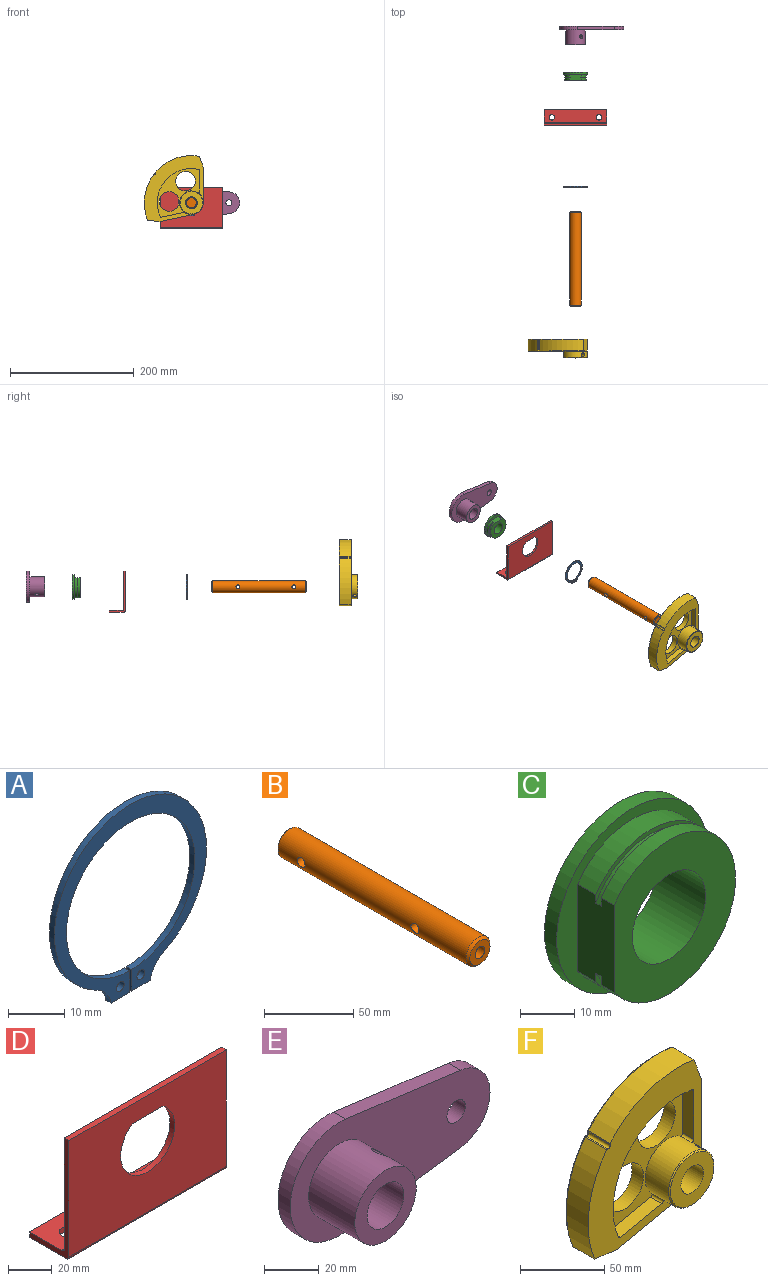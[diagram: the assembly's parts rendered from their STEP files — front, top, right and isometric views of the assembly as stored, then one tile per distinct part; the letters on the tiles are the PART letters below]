
ASSEMBLY  parts=6 mates=5
PART A: 12 faces, bbox 38.3x1.3x40.8 mm
  f0: cylinder r=19.13mm len=38.25mm, axis (0,1,0), area 131.2mm2, adj f1,f8,f10,f11
  f1: cylinder r=6.34mm len=4.3mm, axis (0,1,0), area 6.9mm2, adj f0,f2,f10,f11
  f2: plane 4.67x1.27mm, normal (0,0,-1), area 5.9mm2, adj f1,f3,f10,f11
  f3: plane 4.68x1.27mm, normal (1,0,0), area 5.9mm2, adj f2,f4,f10,f11
  f4: cylinder r=16.15mm len=32.31mm, axis (0,1,0), area 128.3mm2, adj f3,f5,f10,f11
  f5: plane 4.68x1.27mm, normal (-1,0,0), area 5.9mm2, adj f4,f6,f10,f11
  f6: plane 4.67x1.27mm, normal (0,0,-1), area 5.9mm2, adj f5,f8,f10,f11
  f7: cylinder r=0.99mm len=1.98mm, axis (0,1,0), area 7.9mm2, adj f10,f11
  f8: cylinder r=6.34mm len=4.54mm, axis (0,1,0), area 7.5mm2, adj f0,f6,f10,f11
  f9: cylinder r=0.99mm len=1.98mm, axis (0,1,0), area 7.9mm2, adj f10,f11
  f10: plane 40.84x38.25mm, normal (0,-1,0), area 354mm2, adj f0,f1,f2,f3,f4,f5,f6,f7
  f11: plane 40.84x38.25mm, normal (0,1,0), area 354mm2, adj f0,f1,f2,f3,f4,f5,f6,f7
PART B: 9 faces, bbox 19.1x152.4x19.1 mm
  f0: cylinder r=9.53mm len=149.35mm, axis (0,1,0), area 8809.5mm2, adj f3,f4,f5,f6
  f1: plane 16x16mm, normal (0,1,0), area 201.1mm2, adj f3
  f2: plane 16x16mm, normal (0,-1,0), area 153.4mm2, adj f4,f8
  f3: cone r=8mm half-angle=45deg, axis (0,-1,0), area 118.7mm2, adj f0,f1
  f4: cone r=9.53mm half-angle=45deg, axis (0,1,0), area 118.7mm2, adj f0,f2
  f5: cylinder r=3.17mm len=19.05mm, axis (1,0,0), area 369.3mm2, adj f0
  f6: cylinder r=3.17mm len=19.05mm, axis (1,0,0), area 369.3mm2, adj f0
  f7: cone r=0mm half-angle=59deg, axis (0,-1,0), area 55.7mm2, adj f8
  f8: cylinder r=3.9mm len=19.05mm, axis (0,-1,0), area 466.7mm2, adj f2,f7
PART C: 11 faces, bbox 39.6x12.7x39.6 mm
  f0: cylinder r=9.56mm len=19.13mm, axis (0,1,0), area 763.1mm2, adj f3,f9
  f1: cylinder r=19.81mm len=39.62mm, axis (0,1,0), area 395.2mm2, adj f2,f3
  f2: plane 39.62x39.62mm, normal (0,-1,0), area 322.8mm2, adj f1,f4,f5
  f3: plane 39.62x39.62mm, normal (0,1,0), area 945.8mm2, adj f0,f1
  f4: plane 19.67x9.53mm, normal (-1,0,0), area 182mm2, adj f2,f5,f6,f7,f8,f9,f10
  f5: cylinder r=17.4mm len=34.8mm, axis (0,1,0), area 419.9mm2, adj f2,f4,f6
  f6: plane 34.8x31.75mm, normal (0,-1,0), area 87.7mm2, adj f4,f5,f7
  f7: cylinder r=16.4mm len=32.79mm, axis (0,1,0), area 123mm2, adj f4,f6,f10
  f8: cylinder r=17.4mm len=34.8mm, axis (0,1,0), area 296.4mm2, adj f4,f9,f10
  f9: plane 34.8x31.75mm, normal (0,-1,0), area 623mm2, adj f0,f4,f8
  f10: plane 34.8x31.75mm, normal (0,1,0), area 87.7mm2, adj f4,f7,f8
PART D: 14 faces, bbox 101.6x25.4x66.7 mm
  f0: plane 101.6x65.15mm, normal (0,-1,0), area 5707.7mm2, adj f5,f6,f7,f9,f10,f11
  f1: plane 101.6x23.88mm, normal (0,0,-1), area 2306.6mm2, adj f2,f6,f7,f9,f12,f13
  f2: plane 101.6x3.04mm, normal (0,1,0), area 308.6mm2, adj f1,f3,f6,f7
  f3: plane 101.6x20.84mm, normal (0,0,1), area 1997.9mm2, adj f2,f6,f7,f8,f12,f13
  f4: plane 101.6x62.11mm, normal (0,1,0), area 5399mm2, adj f5,f6,f7,f8,f10,f11
  f5: plane 101.6x3.04mm, normal (0,0,1), area 308.6mm2, adj f0,f4,f6,f7
  f6: plane 66.68x25.4mm, normal (-1,0,0), area 270.5mm2, adj f0,f1,f2,f3,f4,f5,f8,f9
  f7: plane 66.68x25.4mm, normal (1,0,0), area 270.5mm2, adj f0,f1,f2,f3,f4,f5,f8,f9
  f8: cylinder r=1.52mm len=101.6mm, axis (1,0,0), area 243.2mm2, adj f3,f4,f6,f7
  f9: cylinder r=1.52mm len=101.6mm, axis (-1,0,0), area 243.2mm2, adj f0,f1,f6,f7
  f10: plane 19.68x3.04mm, normal (0,0,-1), area 59.8mm2, adj f0,f4,f11
  f11: cylinder r=17.41mm len=34.82mm, axis (0,-1,0), area 268.8mm2, adj f0,f4,f10
  f12: cylinder r=4.36mm len=8.71mm, axis (0,0,1), area 83.1mm2, adj f1,f3
  f13: cylinder r=4.36mm len=8.71mm, axis (0,0,1), area 83.1mm2, adj f1,f3
PART E: 14 faces, bbox 103.4x30.2x50.8 mm
  f0: cylinder r=25.4mm len=50.8mm, axis (0,1,0), area 548.8mm2, adj f1,f3,f6,f7
  f1: plane 59.43x7.81mm, normal (0.13,0,-0.99), area 380.6mm2, adj f0,f2,f6,f7
  f2: cylinder r=17.53mm len=34.75mm, axis (0,1,0), area 320.6mm2, adj f1,f3,f6,f7
  f3: plane 59.43x7.81mm, normal (0.13,0,0.99), area 380.6mm2, adj f0,f2,f6,f7
  f4: cylinder r=12.89mm len=25.78mm, axis (0,1,0), area 514.3mm2, adj f7,f11
  f5: cylinder r=4.79mm len=9.58mm, axis (0,1,0), area 191mm2, adj f6,f7
  f6: plane 103.38x50.8mm, normal (0,-1,0), area 3249.2mm2, adj f0,f1,f2,f3,f5,f9
  f7: plane 103.38x50.8mm, normal (0,1,0), area 3518.9mm2, adj f0,f1,f2,f3,f4,f5
  f8: cylinder r=9.55mm len=23.88mm, axis (0,1,0), area 1368.5mm2, adj f10,f11,f12,f13
  f9: cylinder r=15.88mm len=31.75mm, axis (0,1,0), area 2318mm2, adj f6,f10,f12,f13
  f10: plane 31.75x31.75mm, normal (0,-1,0), area 505.2mm2, adj f8,f9
  f11: plane 25.78x25.78mm, normal (0,1,0), area 235.5mm2, adj f4,f8
  f12: cylinder r=3.17mm len=9.31mm, axis (0.6,0,0.8), area 128.3mm2, adj f8,f9
  f13: cylinder r=3.17mm len=9.31mm, axis (0.6,0,0.8), area 128.4mm2, adj f8,f9
PART F: 32 faces, bbox 101.5x30.2x113.3 mm
  f0: cylinder r=19.05mm len=38.1mm, axis (0,1,0), area 2201.4mm2, adj f4,f5,f11,f19,f20,f21,f22,f24
  f1: cylinder r=9.55mm len=30.23mm, axis (0,1,0), area 1749.4mm2, adj f5,f23,f25,f26
  f2: cylinder r=15.88mm len=31.75mm, axis (0,1,0), area 962.7mm2, adj f4,f5
  f3: cylinder r=15.88mm len=31.75mm, axis (0,1,0), area 962.7mm2, adj f4,f5
  f4: plane 78.66x67.98mm, normal (0,-1,0), area 1755.2mm2, adj f0,f2,f3,f6,f7,f8,f9,f10
  f5: plane 106.07x94.49mm, normal (0,1,0), area 6188.1mm2, adj f0,f1,f2,f3,f11,f12,f18,f19
  f6: plane 34.53x9.4mm, normal (-0.21,0,0.98), area 331.8mm2, adj f4,f8,f20,f22
  f7: plane 35.3x9.4mm, normal (-1,0,0), area 331.8mm2, adj f4,f10,f21,f22
  f8: cylinder r=1.52mm len=9.4mm, axis (0,1,0), area 19.5mm2, adj f4,f6,f9,f22
  f9: cylinder r=55.28mm len=77.76mm, axis (0,1,0), area 1142.4mm2, adj f4,f8,f10,f22
  f10: cylinder r=1.52mm len=9.4mm, axis (0,1,0), area 19.5mm2, adj f4,f7,f9,f22
  f11: plane 57.69x19.05mm, normal (1,0,0), area 1099mm2, adj f0,f5,f12,f22
  f12: plane 19.05x17.44mm, normal (0.94,0,0.34), area 353.5mm2, adj f5,f11,f13,f22,f27
  f13: cylinder r=76.2mm len=70.53mm, axis (0,1,0), area 1434.2mm2, adj f12,f14,f22,f27
  f14: cylinder r=0.76mm len=18.29mm, axis (0,1,0), area 17.4mm2, adj f13,f15,f22,f28
  f15: cylinder r=1.52mm len=18.29mm, axis (0,1,0), area 67.8mm2, adj f14,f16,f22,f29
  f16: cylinder r=0.76mm len=18.29mm, axis (0,1,0), area 17.4mm2, adj f15,f17,f22,f30
  f17: cylinder r=76.2mm len=74.3mm, axis (0,1,0), area 1434.2mm2, adj f16,f18,f22,f31
  f18: plane 19.05x18.38mm, normal (-0.14,0,-0.99), area 353.5mm2, adj f5,f17,f19,f22,f31
  f19: plane 56.43x19.05mm, normal (0.21,0,-0.98), area 1099mm2, adj f0,f5,f18,f22
  f20: cylinder r=1.52mm len=9.4mm, axis (0,1,0), area 30.7mm2, adj f0,f4,f6,f22
  f21: cylinder r=1.52mm len=9.4mm, axis (0,1,0), area 30.7mm2, adj f0,f4,f7,f22
  f22: plane 106.83x95.25mm, normal (0,-1,0), area 3702.8mm2, adj f0,f6,f7,f8,f9,f10,f11,f12
  f23: plane 36.58x36.58mm, normal (0,-1,0), area 764.2mm2, adj f1,f24
  f24: cone r=18.29mm half-angle=45deg, axis (0,1,0), area 126.4mm2, adj f0,f23
  f25: cylinder r=3.17mm len=11.8mm, axis (-0.63,0,-0.78), area 192.2mm2, adj f0,f1
  f26: cylinder r=3.17mm len=11.8mm, axis (-0.63,0,-0.78), area 192.2mm2, adj f0,f1
  f27: torus R=75.44mm, axis (0,-1,0), area 93.7mm2, adj f5,f12,f13,f28
  f28: sphere r=0.76mm, area 0.7mm2, adj f14,f27,f29
  f29: torus R=2.29mm, axis (0,-1,0), area 5.2mm2, adj f5,f15,f28,f30
  f30: sphere r=0.76mm, area 0.7mm2, adj f16,f29,f31
  f31: torus R=75.44mm, axis (0,-1,0), area 93.7mm2, adj f5,f17,f18,f30
PLACE A t=(-1.3,-93.03,37.02)mm
PLACE B rot(axis=(0,0,1),180deg) t=(-1.3,-286.67,37.02)mm
PLACE C rot(axis=(0,1,0),90deg) t=(-1.3,91.52,37.02)mm
PLACE D t=(-1.3,5.94,-4.25)mm fixed
PLACE E t=(-1.3,166.2,37.02)mm
PLACE F t=(-1.3,-340.27,37.02)mm
MATE slider C.f0 <-> D.f11  axis (0,1,0) through (-1.3,78.82,37.02)mm
MATE slider A.f4 <-> C.f0  axis (0,-1,0) through (-1.3,-94.3,37.02)mm
MATE slider E.f9 <-> C.f0  axis (0,-1,0) through (-1.3,135.97,37.02)mm
MATE slider B.f0 <-> D.f11  axis (0,-1,0) through (-1.3,-135.8,37.02)mm
MATE slider F.f0 <-> B.f0  axis (0,1,0) through (-1.3,-340.27,37.02)mm
